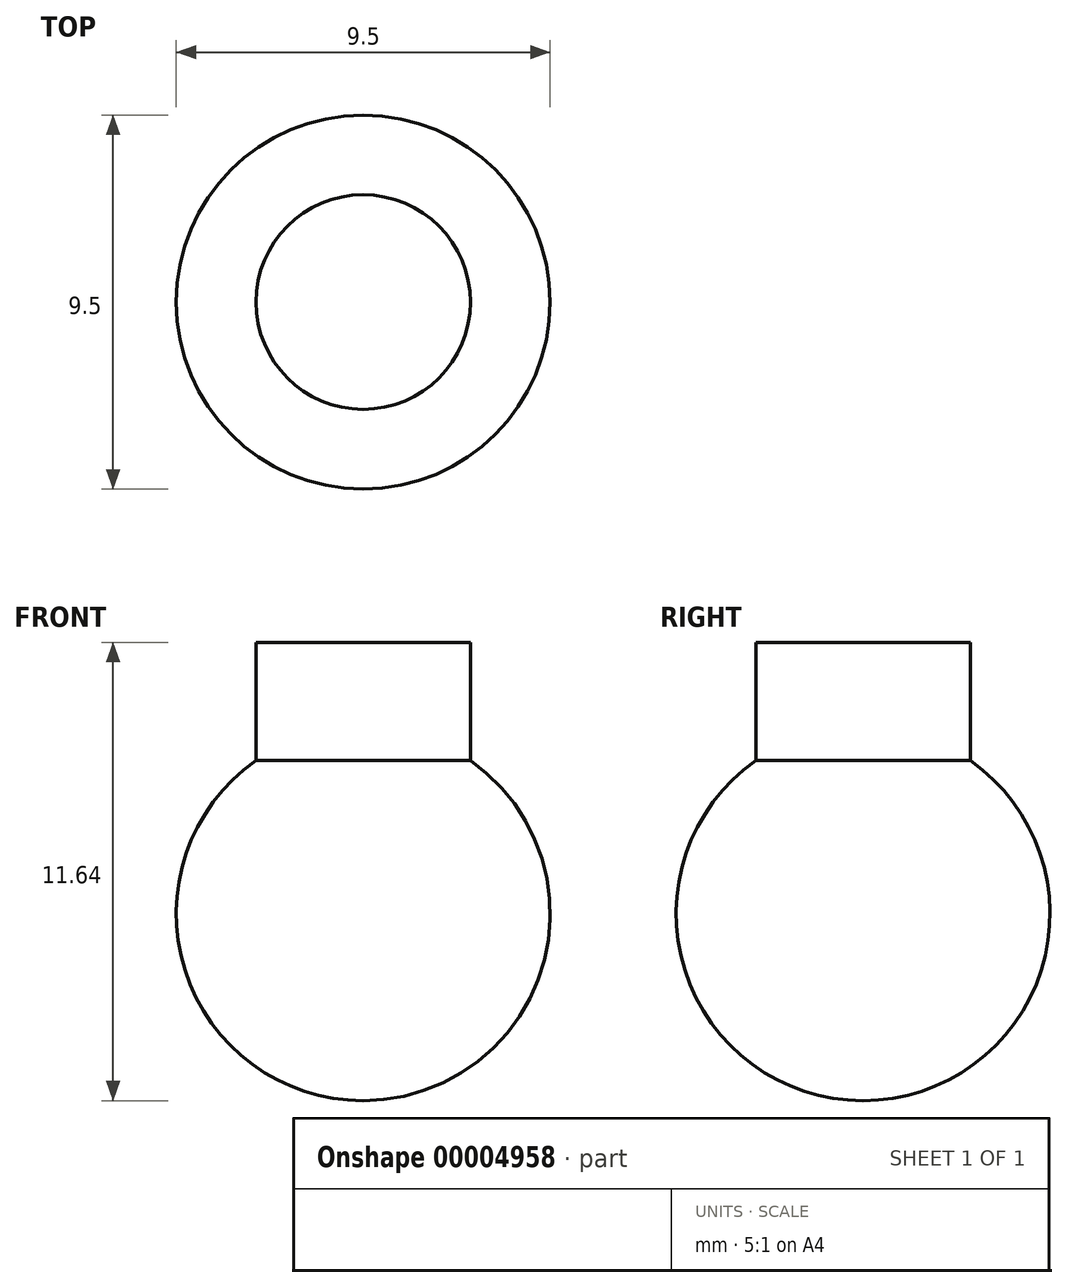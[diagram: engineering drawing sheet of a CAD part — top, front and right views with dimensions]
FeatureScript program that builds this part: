
annotation { "Feature Type Name" : "Feature", "Feature Type Description" : "" }
export const myFeature = defineFeature(function(context is Context, id is Id, definition is map)
    precondition{}
    {
        {
            var Q0;
            Q0=qCreatedBy(makeId("Front.planeOp"),FACE);
            var sketch = newSketch(context, id + "F0", { "sketchPlane" : qUnion([Q0])});
            skLineSegment(sketch, "E0", {"start": v(0, 0) * mm, "end": v(0, -11.64) * mm});
            skLineSegment(sketch, "E1", {"start": v(0, 0) * mm, "end": v(2.72, 0) * mm});
            skLineSegment(sketch, "E2", {"start": v(2.72, 0) * mm, "end": v(2.72, -3) * mm});
            skArc(sketch, "E3", {"start": v(0, -11.64) * mm, "mid": v(4.53, -8.32) * mm, "end": v(2.73, -3) * mm});
            skLineSegment(sketch, "E4", {"start": v(0, -11.64) * mm, "end": v(-11.6, -11.64) * mm, "construction": true});
            skSolve(sketch);
        }
        {
            var Q0;
            Q0 = qSketchRegion(id + "F0", true);
            var Q1;
            Q1=sQuery(id+"F0.wireOp",EDGE,"E0");
            revolve(context, id + "F1", {"entities" : qUnion([Q0]), "axis" : qUnion([Q1]), "revolveType" : RevolveType.FULL});
        }
    });
